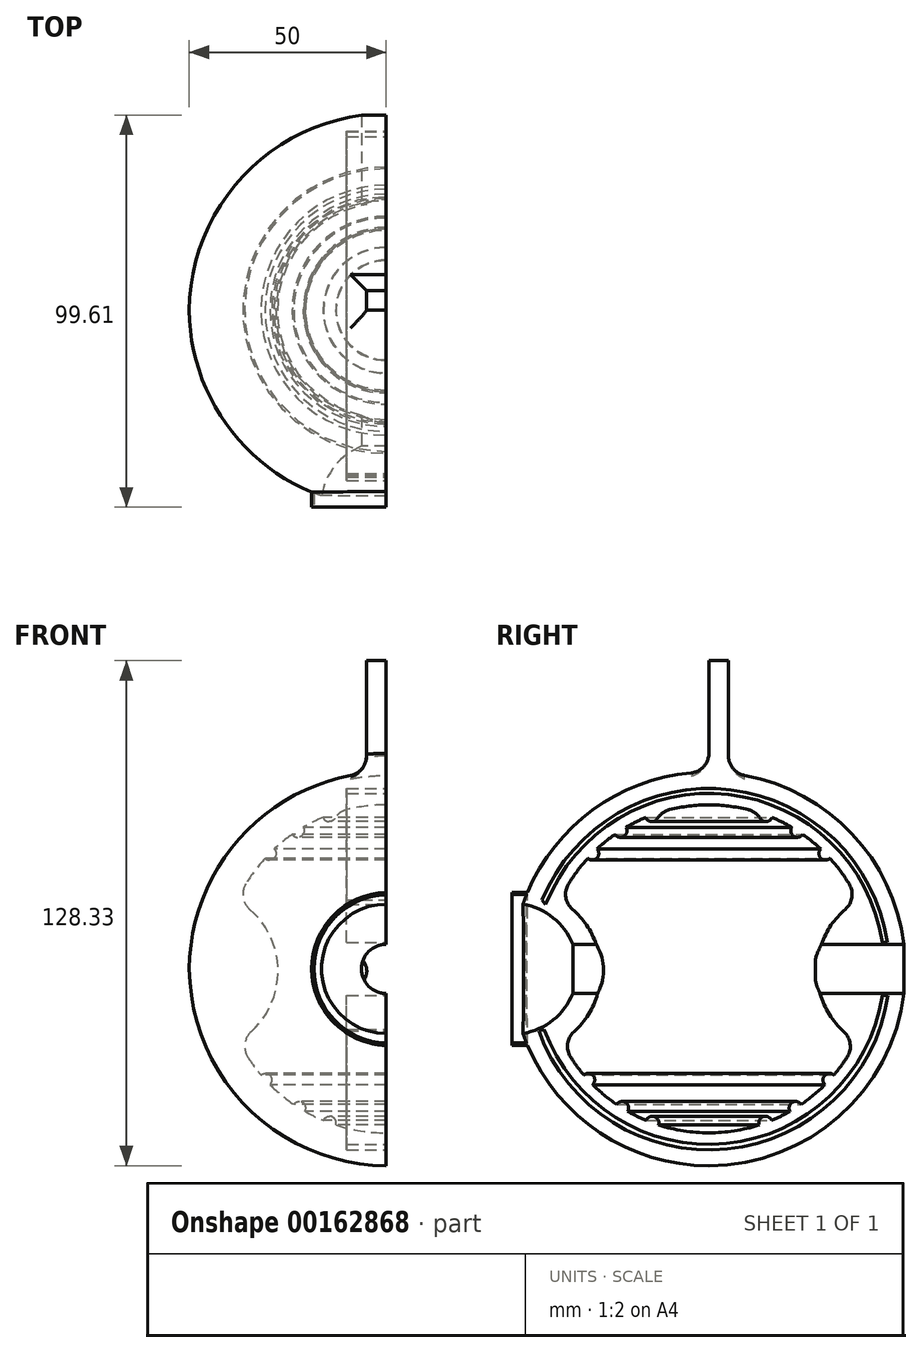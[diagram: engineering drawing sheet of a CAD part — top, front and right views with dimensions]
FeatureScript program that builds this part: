
annotation { "Feature Type Name" : "Feature", "Feature Type Description" : "" }
export const myFeature = defineFeature(function(context is Context, id is Id, definition is map)
    precondition{}
    {
        {
            assignVariable(context, id + "F0", {"name" : "Width", "anyValue" : 100 * mm});
        }
        {
            var Q0;
            Q0=qCreatedBy(makeId("Top.planeOp"),FACE);
            var sketch = newSketch(context, id + "F1", { "sketchPlane" : qUnion([Q0])});
            skArc(sketch, "E0", {"start": v(0, 50) * mm, "mid": v(-35.25, 35.25) * mm, "end": v(-50, 0) * mm});
            skLineSegment(sketch, "E1", {"start": v(-50, 0) * mm, "end": v(0, 0) * mm});
            skLineSegment(sketch, "E2", {"start": v(0, -25.02) * mm, "end": v(0, 61.17) * mm});
            skPoint(sketch, "E3.orphan", {"position": v(50.73, 0) * mm});
            skSolve(sketch);
        }
        {
            var Q0;
            Q0=qSketchRegion(id+"F1",true);
            var Q1;
            Q1=sQuery(id+"F1.wireOp",EDGE,"E1");
            revolve(context, id + "F2", {"entities" : qUnion([Q0]), "axis" : qUnion([Q1]), "revolveType" : RevolveType.FULL});
        }
        {
            var Q0;
            Q0=qCreatedBy(makeId("Front.planeOp"),FACE);
            cPlane(context, id + "F3", {"entities" : qUnion([Q0]), "cplaneType" : CPlaneType.OFFSET, "offset" : 50 * mm, "width" : 150 * mm, "height" : 150 * mm});
        }
        {
            var Q0;
            Q0=qCreatedBy(id+"F3.planeOp",FACE);
            var sketch = newSketch(context, id + "F4", { "sketchPlane" : qUnion([Q0])});
            skArc(sketch, "E4", {"start": v(0, 16.67) * mm, "mid": v(-16.67, 0) * mm, "end": v(0, -16.67) * mm});
            skLineSegment(sketch, "E5", {"start": v(0, 23.26) * mm, "end": v(0, -27.2) * mm});
            skSolve(sketch);
        }
        {
            var Q0;
            Q0=qSketchRegion(id+"F4",true);
            var Q1;
            Q1=sQuery(id+"F4.wireOp",EDGE,"E5");
            revolve(context, id + "F5", {"operationType" : NewBodyOperationType.REMOVE, "entities" : qUnion([Q0]), "axis" : qUnion([Q1]), "revolveType" : RevolveType.FULL, "oppositeDirection" : true});
        }
        {
            var Q0;
            Q0=makeQuery(id+"F2.opRevolve","SWEPT_FACE",FACE,{"disambiguationData":[OSD([sQuery(id+"F1.wireOp",EDGE,"E2")])]});
            var sketch = newSketch(context, id + "F6", { "sketchPlane" : qUnion([Q0])});
            skArc(sketch, "E6", {"start": v(-37.42, -18.32) * mm, "mid": v(-34.86, -22.82) * mm, "end": v(-31.76, -26.97) * mm});
            skArc(sketch, "E7", {"start": v(-37.42, -18.32) * mm, "mid": v(-27.48, -0.33) * mm, "end": v(-37.85, 17.43) * mm});
            skLineSegment(sketch, "E8", {"start": v(0, 59.66) * mm, "end": v(0, -56.85) * mm});
            skArc(sketch, "E9.trimOffspring", {"start": v(0, 41.67) * mm, "mid": v(-6.53, 41.15) * mm, "end": v(-12.9, 39.62) * mm});
            skArc(sketch, "E10", {"start": v(-29.5, -29.43) * mm, "mid": v(-29.43, -27.1) * mm, "end": v(-31.76, -26.97) * mm});
            skArc(sketch, "E11", {"start": v(-12.78, -39.66) * mm, "mid": v(-13.78, -37.55) * mm, "end": v(-15.91, -38.5) * mm});
            skArc(sketch, "E12", {"start": v(-30.77, 28.1) * mm, "mid": v(-28.44, 28.13) * mm, "end": v(-28.43, 30.46) * mm});
            skArc(sketch, "E13", {"start": v(-16.03, 38.46) * mm, "mid": v(-13.9, 37.5) * mm, "end": v(-12.9, 39.62) * mm});
            skArc(sketch, "E14", {"start": v(-23.86, 34.16) * mm, "mid": v(-21.57, 33.68) * mm, "end": v(-21.05, 35.96) * mm});
            skArc(sketch, "E15", {"start": v(-20.62, -36.2) * mm, "mid": v(-21.17, -33.94) * mm, "end": v(-23.45, -34.44) * mm});
            skArc(sketch, "E16.trimOffspring", {"start": v(-12.78, -39.66) * mm, "mid": v(-6.47, -41.16) * mm, "end": v(0, -41.67) * mm});
            skArc(sketch, "E17.trimOffspring", {"start": v(-20.62, -36.2) * mm, "mid": v(-18.3, -37.43) * mm, "end": v(-15.91, -38.5) * mm});
            skArc(sketch, "E18.trimOffspring", {"start": v(-29.5, -29.43) * mm, "mid": v(-26.6, -32.08) * mm, "end": v(-23.45, -34.44) * mm});
            skArc(sketch, "E19.trimOffspring", {"start": v(-23.86, 34.16) * mm, "mid": v(-26.2, 32.4) * mm, "end": v(-28.43, 30.46) * mm});
            skArc(sketch, "E20.trimOffspring", {"start": v(-16.03, 38.46) * mm, "mid": v(-18.58, 37.3) * mm, "end": v(-21.05, 35.96) * mm});
            skArc(sketch, "E21.trimOffspring", {"start": v(-30.77, 28.1) * mm, "mid": v(-34.72, 23.03) * mm, "end": v(-37.85, 17.43) * mm});
            skSolve(sketch);
        }
        {
            var Q0;
            Q0=qSketchRegion(id+"F6",true);
            var Q1;
            Q1=sQuery(id+"F6.wireOp",EDGE,"E8");
            revolve(context, id + "F7", {"operationType" : NewBodyOperationType.REMOVE, "entities" : qUnion([Q0]), "axis" : qUnion([Q1]), "revolveType" : RevolveType.FULL, "oppositeDirection" : true});
        }
        {
            var Q0;
            Q0=makeQuery(id+"F2.opRevolve","SWEPT_FACE",FACE,{"disambiguationData":[OSD([sQuery(id+"F1.wireOp",EDGE,"E2")])]});
            var sketch = newSketch(context, id + "F8", { "sketchPlane" : qUnion([Q0])});
            skLineSegment(sketch, "E22.top", {"start": v(50.36, 6.25) * mm, "end": v(27.03, 6.25) * mm});
            skLineSegment(sketch, "E22.left", {"start": v(50.36, 0) * mm, "end": v(50.36, 6.25) * mm});
            skLineSegment(sketch, "E22.right", {"start": v(27.03, 0) * mm, "end": v(27.03, 6.25) * mm});
            skPoint(sketch, "E22.middle", {"position": v(38.7, 0) * mm});
            skLineSegment(sketch, "E23", {"start": v(50.36, 0) * mm, "end": v(22.73, 0) * mm});
            skPoint(sketch, "E24.orphan", {"position": v(50.36, -6.25) * mm});
            skPoint(sketch, "E25.orphan", {"position": v(27.03, -6.25) * mm});
            skSolve(sketch);
        }
        {
            var Q0;
            Q0=qSketchRegion(id+"F8",true);
            var Q1;
            Q1=sQuery(id+"F8.wireOp",EDGE,"E23");
            revolve(context, id + "F9", {"operationType" : NewBodyOperationType.REMOVE, "entities" : qUnion([Q0]), "axis" : qUnion([Q1]), "revolveType" : RevolveType.FULL, "oppositeDirection" : true});
        }
        {
            var Q0;
            Q0=makeQuery(id+"F7.boolean.opBoolean","COPY",EDGE,{"derivedFrom":makeQuery(id+"F7.opRevolve","SWEPT_EDGE",EDGE,{"disambiguationData":[OSD([sQuery(id+"F6.wireOp",EDGE,"E7"),sQuery(id+"F6.wireOp",EDGE,"E9.trimOffspring")])]})});
            var Q1;
            Q1=makeQuery(id+"F7.boolean.opBoolean","COPY",EDGE,{"derivedFrom":makeQuery(id+"F7.opRevolve","SWEPT_EDGE",EDGE,{"disambiguationData":[OSD([sQuery(id+"F6.wireOp",EDGE,"E6"),sQuery(id+"F6.wireOp",EDGE,"E7")])]})});
            fillet(context, id + "F10", {"entities" : qUnion([Q0, Q1]), "radius" : 5 * mm, "tangentPropagation" : true, "allowEdgeOverflow" : false});
        }
        {
            var Q0;
            Q0=qCreatedBy(id+"F3.planeOp",FACE);
            var sketch = newSketch(context, id + "F11", { "sketchPlane" : qUnion([Q0])});
            skCircle(sketch, "E26", {"center": v(0, 0) * mm, "radius": 6.25 * mm});
            skSolve(sketch);
        }
        {
            var Q0;
            Q0=qSketchRegion(id+"F11",true);
            extrude(context, id + "F12", {"entities" : qUnion([Q0]), "operationType" : NewBodyOperationType.REMOVE, "oppositeDirection" : true, "depth" : getVariable(context, 'Width') / 3});
        }
        {
            var Q0;
            {var subQ0=sQuery(id+"F6.wireOp",EDGE,"E9.trimOffspring");Q0=makeQuery(id+"F12.boolean.opBoolean","SPLIT",FACE,{"disambiguationData":[TD([makeQuery(id+"F7.boolean.opBoolean","COPY",FACE,{"derivedFrom":makeQuery(id+"F7.opRevolve","SWEPT_FACE",FACE,{"disambiguationData":[OSD([subQ0])]})})])],"derivedFrom":makeQuery(id+"F2.opRevolve","SWEPT_FACE",FACE,{"disambiguationData":[OSD([sQuery(id+"F1.wireOp",EDGE,"E2")])]})});}
            var sketch = newSketch(context, id + "F13", { "sketchPlane" : qUnion([Q0])});
            skArc(sketch, "E27", {"start": v(44.07, 6.75) * mm, "mid": v(5.02, 44.3) * mm, "end": v(-41.44, 16.43) * mm});
            skLineSegment(sketch, "E28", {"start": v(52, -6.75) * mm, "end": v(44.07, -6.75) * mm});
            skArc(sketch, "E29.trimOffspring", {"start": v(-41.87, -15.32) * mm, "mid": v(4.42, -44.36) * mm, "end": v(44.07, -6.75) * mm});
            skArc(sketch, "E30.0", {"start": v(45.33, 6.75) * mm, "mid": v(5.58, 45.5) * mm, "end": v(-42.36, 17.5) * mm});
            skArc(sketch, "E31.0", {"start": v(-43.21, -15.8) * mm, "mid": v(4.79, -45.76) * mm, "end": v(45.55, -6.52) * mm});
            skLineSegment(sketch, "E32", {"start": v(-42.36, 17.5) * mm, "end": v(-41.44, 16.43) * mm});
            skLineSegment(sketch, "E33", {"start": v(45.33, 6.75) * mm, "end": v(44.07, 6.75) * mm});
            skLineSegment(sketch, "E34", {"start": v(45.55, -6.52) * mm, "end": v(44.07, -6.75) * mm});
            skLineSegment(sketch, "E35", {"start": v(-41.87, -15.32) * mm, "end": v(-43.21, -15.8) * mm});
            skSolve(sketch);
        }
        {
            var Q0;
            Q0=makeQuery(id+"F13.imprint","IMPRINT",FACE,{"disambiguationData":[TD([[makeQuery(id+"F13.imprint","IMPRINT",EDGE,{"derivedFrom":sQuery(id+"F13.wireOp",EDGE,"E27")}),-1.0]])]});
            extrude(context, id + "F14", {"entities" : qUnion([Q0]), "operationType" : NewBodyOperationType.REMOVE, "oppositeDirection" : true, "depth" : 10 * mm});
        }
        {
            var Q0;
            Q0=makeQuery(id+"F13.imprint","IMPRINT",FACE,{"disambiguationData":[TD([[makeQuery(id+"F13.imprint","IMPRINT",EDGE,{"derivedFrom":sQuery(id+"F13.wireOp",EDGE,"E29.trimOffspring")}),-1.0]])]});
            extrude(context, id + "F15", {"entities" : qUnion([Q0]), "operationType" : NewBodyOperationType.REMOVE, "oppositeDirection" : true, "depth" : 10 * mm});
        }
        {
            var Q0;
            Q0=qCreatedBy(makeId("Top.planeOp"),FACE);
            cPlane(context, id + "F16", {"entities" : qUnion([Q0]), "cplaneType" : CPlaneType.OFFSET, "offset" : getVariable(context, 'Width') / 2, "width" : 150 * mm, "height" : 150 * mm});
        }
        {
            var Q0;
            Q0=qCreatedBy(id+"F16.planeOp",FACE);
            var sketch = newSketch(context, id + "F17", { "sketchPlane" : qUnion([Q0])});
            skLineSegment(sketch, "E36.bottom", {"start": v(0, 0) * mm, "end": v(-5, 0) * mm});
            skLineSegment(sketch, "E36.top", {"start": v(0, 5) * mm, "end": v(-5, 5) * mm});
            skLineSegment(sketch, "E36.left", {"start": v(0, 0) * mm, "end": v(0, 5) * mm});
            skLineSegment(sketch, "E36.right", {"start": v(-5, 0) * mm, "end": v(-5, 5) * mm});
            skSolve(sketch);
        }
        {
            var Q0;
            Q0 = qSketchRegion(id + "F17", true);
            extrude(context, id + "F18", {"entities" : qUnion([Q0]), "operationType" : NewBodyOperationType.ADD, "endBound" : BoundingType.SYMMETRIC, "depth" : getVariable(context, 'Width') / 15});
        }
        {
            var Q0;
            Q0=makeQuery(id+"F18.opExtrude","CAP_FACE",FACE,{"disambiguationData":[OSD([sQuery(id+"F17.wireOp",EDGE,"E36.bottom"),sQuery(id+"F17.wireOp",EDGE,"E36.top"),sQuery(id+"F17.wireOp",EDGE,"E36.left"),sQuery(id+"F17.wireOp",EDGE,"E36.right")])],"isStart":false});
            var sketch = newSketch(context, id + "F19", { "sketchPlane" : qUnion([Q0])});
            skLineSegment(sketch, "E37.bottom", {"start": v(-5, 5) * mm, "end": v(0, 5) * mm});
            skLineSegment(sketch, "E37.top", {"start": v(-5, 0) * mm, "end": v(0, 0) * mm});
            skLineSegment(sketch, "E37.left", {"start": v(-5, 5) * mm, "end": v(-5, 0) * mm});
            skLineSegment(sketch, "E37.right", {"start": v(0, 5) * mm, "end": v(0, 0) * mm});
            skSolve(sketch);
        }
        {
            var Q0;
            Q0 = qSketchRegion(id + "F19", true);
            extrude(context, id + "F20", {"entities" : qUnion([Q0]), "operationType" : NewBodyOperationType.ADD, "depth" : getVariable(context, 'Width') / 4});
        }
        {
            var Q0;
            Q0=qCreatedBy(id+"F3.planeOp",FACE);
            var sketch = newSketch(context, id + "F21", { "sketchPlane" : qUnion([Q0])});
            skArc(sketch, "E38", {"start": v(0, 18.86) * mm, "mid": v(-18.33, 0) * mm, "end": v(0, -18.86) * mm});
            skArc(sketch, "E39", {"start": v(0, 19.43) * mm, "mid": v(-18.9, 0) * mm, "end": v(0, -19.43) * mm});
            skLineSegment(sketch, "E40", {"start": v(0, 19.43) * mm, "end": v(0, 18.86) * mm});
            skPoint(sketch, "E41.orphan", {"position": v(0, 31.25) * mm});
            skLineSegment(sketch, "E42.trimOffspring", {"start": v(0, -18.86) * mm, "end": v(0, -19.43) * mm});
            skSolve(sketch);
        }
        {
            var Q0;
            Q0 = qSketchRegion(id + "F21", true);
            extrude(context, id + "F22", {"entities" : qUnion([Q0]), "operationType" : NewBodyOperationType.ADD, "oppositeDirection" : true, "depth" : getVariable(context, 'Width') / 20});
        }
        {
            var Q0;
            Q0=makeQuery(id+"F18.boolean.opBoolean","INTERSECT",EDGE,{"derivedFrom":[makeQuery(id+"F2.opRevolve","SWEPT_FACE",FACE,{"disambiguationData":[OSD([sQuery(id+"F1.wireOp",EDGE,"E0")])]}),makeQuery(id+"F18.opExtrude","SWEPT_FACE",FACE,{"disambiguationData":[OSD([sQuery(id+"F17.wireOp",EDGE,"E36.top")])]})]});
            var Q1;
            Q1=makeQuery(id+"F18.boolean.opBoolean","INTERSECT",EDGE,{"derivedFrom":[makeQuery(id+"F2.opRevolve","SWEPT_FACE",FACE,{"disambiguationData":[OSD([sQuery(id+"F1.wireOp",EDGE,"E0")])]}),makeQuery(id+"F18.opExtrude","SWEPT_FACE",FACE,{"disambiguationData":[OSD([sQuery(id+"F17.wireOp",EDGE,"E36.right")])]})]});
            var Q2;
            Q2=makeQuery(id+"F18.boolean.opBoolean","INTERSECT",EDGE,{"derivedFrom":[makeQuery(id+"F2.opRevolve","SWEPT_FACE",FACE,{"disambiguationData":[OSD([sQuery(id+"F1.wireOp",EDGE,"E0")])]}),makeQuery(id+"F18.opExtrude","SWEPT_FACE",FACE,{"disambiguationData":[OSD([sQuery(id+"F17.wireOp",EDGE,"E36.bottom")])]})]});
            fillet(context, id + "F23", {"entities" : qUnion([Q0, Q1, Q2]), "radius" : 5 * mm, "tangentPropagation" : true, "allowEdgeOverflow" : false});
        }
    });
